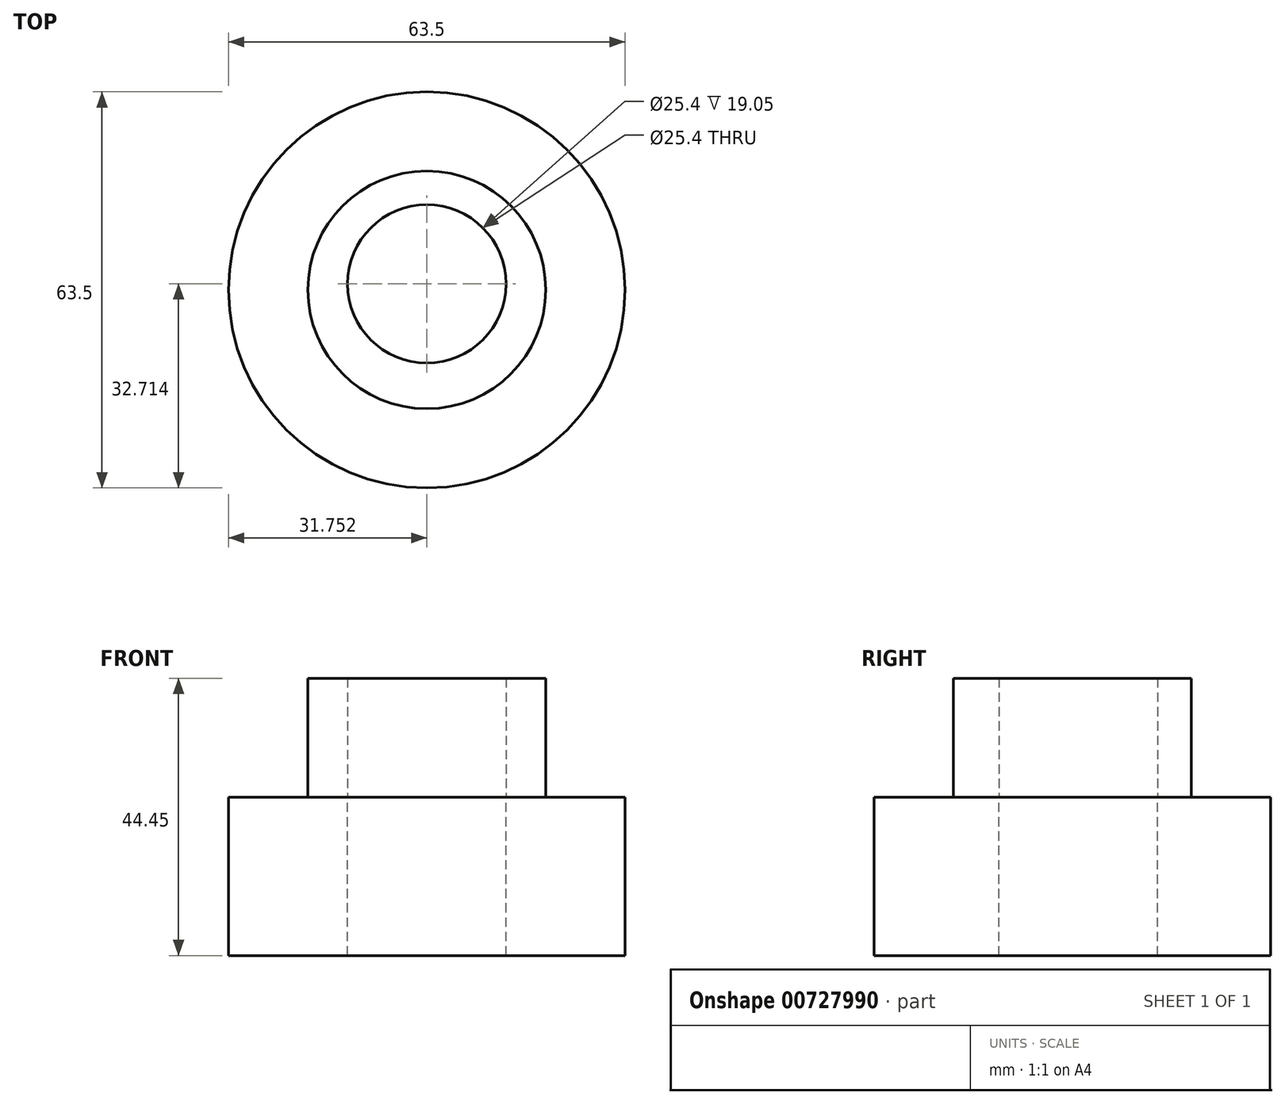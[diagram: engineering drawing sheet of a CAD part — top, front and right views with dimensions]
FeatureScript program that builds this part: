
annotation { "Feature Type Name" : "Feature", "Feature Type Description" : "" }
export const myFeature = defineFeature(function(context is Context, id is Id, definition is map)
    precondition{}
    {
        {
            var Q0;
            Q0=qCreatedBy(makeId("Top.planeOp"),FACE);
            var sketch = newSketch(context, id + "F0", { "sketchPlane" : qUnion([Q0])});
            skCircle(sketch, "E0", {"center": v(0.36, -0.12) * mm, "radius": 31.75 * mm});
            skSolve(sketch);
        }
        {
            var Q0;
            Q0 = qSketchRegion(id + "F0", true);
            extrude(context, id + "F1", {"entities" : qUnion([Q0]), "depth" : 25.4 * mm, "offsetDistance" : 25.4 * mm});
        }
        {
            var Q0;
            Q0=makeQuery(id+"F1.opExtrude","CAP_FACE",FACE,{"disambiguationData":[OSD([sQuery(id+"F0.wireOp",EDGE,"E0")])],"isStart":false});
            var sketch = newSketch(context, id + "F2", { "sketchPlane" : qUnion([Q0])});
            skCircle(sketch, "E1", {"center": v(0.36, -0.12) * mm, "radius": 19.05 * mm});
            skSolve(sketch);
        }
        {
            var Q0;
            Q0 = qSketchRegion(id + "F2", true);
            extrude(context, id + "F3", {"entities" : qUnion([Q0]), "depth" : 19.05 * mm, "offsetDistance" : 25.4 * mm});
        }
        {
            var Q0;
            Q0=makeQuery(id+"F2.imprint","IMPRINT",FACE,{"disambiguationData":[TD([[makeQuery(id+"F2.imprint","IMPRINT",EDGE,{"derivedFrom":sQuery(id+"F2.wireOp",EDGE,"E1")}),1.0]])]});
            var sketch = newSketch(context, id + "F4", { "sketchPlane" : qUnion([Q0])});
            skCircle(sketch, "E2", {"center": v(0.36, 0.84) * mm, "radius": 12.7 * mm});
            skSolve(sketch);
        }
        {
            var Q0;
            Q0 = qSketchRegion(id + "F4", true);
            extrude(context, id + "F5", {"entities" : qUnion([Q0]), "operationType" : NewBodyOperationType.REMOVE, "oppositeDirection" : true, "depth" : 25.4 * mm, "offsetDistance" : 25.4 * mm});
        }
        {
            var Q0;
            Q0 = qSketchRegion(id + "F4", true);
            extrude(context, id + "F6", {"entities" : qUnion([Q0]), "operationType" : NewBodyOperationType.REMOVE, "depth" : 25.4 * mm, "offsetDistance" : 25.4 * mm});
        }
    });
